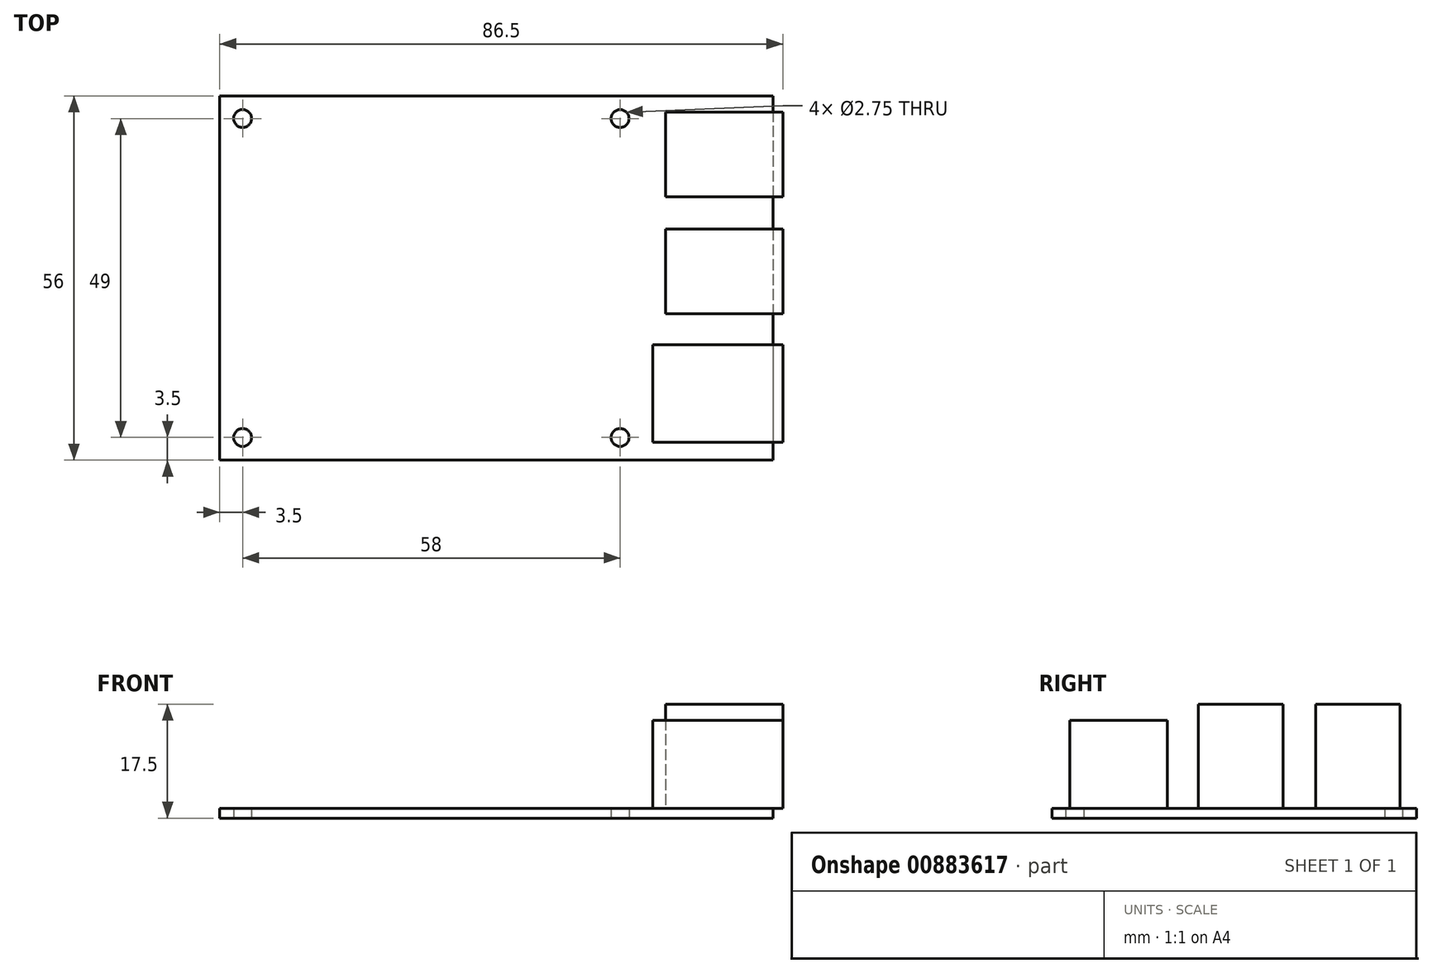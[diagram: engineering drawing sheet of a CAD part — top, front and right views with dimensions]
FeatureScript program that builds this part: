
annotation { "Feature Type Name" : "Feature", "Feature Type Description" : "" }
export const myFeature = defineFeature(function(context is Context, id is Id, definition is map)
    precondition{}
    {
        {
            var Q0;
            Q0=qCreatedBy(makeId("Top.planeOp"),FACE);
            var sketch = newSketch(context, id + "F0", { "sketchPlane" : qUnion([Q0])});
            skLineSegment(sketch, "E0.bottom", {"start": v(0, 56) * mm, "end": v(85, 56) * mm});
            skLineSegment(sketch, "E0.top", {"start": v(0, 0) * mm, "end": v(85, 0) * mm});
            skLineSegment(sketch, "E0.left", {"start": v(0, 56) * mm, "end": v(0, 0) * mm});
            skLineSegment(sketch, "E0.right", {"start": v(85, 56) * mm, "end": v(85, 0) * mm});
            skCircle(sketch, "E1", {"center": v(3.5, 52.5) * mm, "radius": 1.38 * mm});
            skCircle(sketch, "E2", {"center": v(3.5, 3.5) * mm, "radius": 1.38 * mm});
            skCircle(sketch, "E3", {"center": v(61.5, 3.5) * mm, "radius": 1.37 * mm});
            skCircle(sketch, "E4", {"center": v(61.5, 52.5) * mm, "radius": 1.37 * mm});
            skLineSegment(sketch, "E5", {"start": v(3.5, 52.5) * mm, "end": v(61.5, 52.5) * mm, "construction": true});
            skLineSegment(sketch, "E6", {"start": v(61.5, 52.5) * mm, "end": v(61.5, 3.5) * mm, "construction": true});
            skSolve(sketch);
        }
        {
            var Q0;
            {var subQ15=sQuery(id+"F0.wireOp",EDGE,"E0.bottom");Q0=makeQuery(id+"F0.imprint","IMPRINT",FACE,{"disambiguationData":[TD([[makeQuery(id+"F0.imprint","IMPRINT",EDGE,{"derivedFrom":subQ15}),-1.0]])]});}
            var Q1;
            {var subQ5=sQuery(id+"F0.wireOp",EDGE,"uZb7aYxC-zsMW-nidB-drXf-hPC2NGSKKxi8.left");Q1=makeQuery(id+"F0.imprint","IMPRINT",FACE,{"disambiguationData":[TD([[makeQuery(id+"F0.imprint","IMPRINT",EDGE,{"derivedFrom":subQ5}),-1.0]])]});}
            var Q2;
            {var subQ5=sQuery(id+"F0.wireOp",EDGE,"CbbDYCzH-yuqy-8fo1-o1oq-vRqS8r6QZwP0.left");Q2=makeQuery(id+"F0.imprint","IMPRINT",FACE,{"disambiguationData":[TD([[makeQuery(id+"F0.imprint","IMPRINT",EDGE,{"derivedFrom":subQ5}),-1.0]])]});}
            var Q3;
            {var subQ5=sQuery(id+"F0.wireOp",EDGE,"Eq4EePK6-Jx8p-WvZy-9MCs-DtvyUnJVBhWV.left");Q3=makeQuery(id+"F0.imprint","IMPRINT",FACE,{"disambiguationData":[TD([[makeQuery(id+"F0.imprint","IMPRINT",EDGE,{"derivedFrom":subQ5}),-1.0]])]});}
            extrude(context, id + "F1", {"entities" : qUnion([Q0, Q1, Q2, Q3]), "depth" : 1.5 * mm, "offsetDistance" : 25 * mm});
        }
        {
            var Q0;
            Q0=makeQuery(id+"F1.opExtrude","CAP_FACE",FACE,{"disambiguationData":[OSD([sQuery(id+"F0.wireOp",EDGE,"E0.bottom"),sQuery(id+"F0.wireOp",EDGE,"E0.top"),sQuery(id+"F0.wireOp",EDGE,"E0.left"),sQuery(id+"F0.wireOp",EDGE,"E0.right"),sQuery(id+"F0.wireOp",EDGE,"E1"),sQuery(id+"F0.wireOp",EDGE,"E2"),sQuery(id+"F0.wireOp",EDGE,"E3"),sQuery(id+"F0.wireOp",EDGE,"E4")])],"isStart":false});
            cPlane(context, id + "F2", {"entities" : qUnion([Q0]), "cplaneType" : CPlaneType.OFFSET, "offset" : 0 * mm, "width" : 150 * mm, "height" : 150 * mm});
        }
        {
            var Q0;
            Q0=qCreatedBy(id+"F2.planeOp",FACE);
            var sketch = newSketch(context, id + "F3", { "sketchPlane" : qUnion([Q0])});
            skLineSegment(sketch, "E7.bottom", {"start": v(68.5, 53.5) * mm, "end": v(86.5, 53.5) * mm});
            skLineSegment(sketch, "E7.top", {"start": v(68.5, 40.5) * mm, "end": v(86.5, 40.5) * mm});
            skLineSegment(sketch, "E7.left", {"start": v(68.5, 53.5) * mm, "end": v(68.5, 40.5) * mm});
            skLineSegment(sketch, "E7.right", {"start": v(86.5, 53.5) * mm, "end": v(86.5, 40.5) * mm});
            skLineSegment(sketch, "E8.bottom", {"start": v(68.5, 35.5) * mm, "end": v(86.5, 35.5) * mm});
            skLineSegment(sketch, "E8.top", {"start": v(68.5, 22.5) * mm, "end": v(86.5, 22.5) * mm});
            skLineSegment(sketch, "E8.left", {"start": v(68.5, 35.5) * mm, "end": v(68.5, 22.5) * mm});
            skLineSegment(sketch, "E8.right", {"start": v(86.5, 35.5) * mm, "end": v(86.5, 22.5) * mm});
            skLineSegment(sketch, "E9.bottom", {"start": v(66.5, 17.75) * mm, "end": v(86.5, 17.75) * mm});
            skLineSegment(sketch, "E9.top", {"start": v(66.5, 2.75) * mm, "end": v(86.5, 2.75) * mm});
            skLineSegment(sketch, "E9.left", {"start": v(66.5, 17.75) * mm, "end": v(66.5, 2.75) * mm});
            skLineSegment(sketch, "E9.right", {"start": v(86.5, 17.75) * mm, "end": v(86.5, 2.75) * mm});
            skPoint(sketch, "E10", {"position": v(68.5, 47) * mm});
            skPoint(sketch, "E11", {"position": v(68.5, 29) * mm});
            skPoint(sketch, "E12", {"position": v(66.5, 10.25) * mm});
            skSolve(sketch);
        }
        {
            var Q0;
            Q0=makeQuery(id+"F3.imprint","IMPRINT",FACE,{"disambiguationData":[TD([[makeQuery(id+"F3.imprint","IMPRINT",EDGE,{"derivedFrom":sQuery(id+"F3.wireOp",EDGE,"E7.bottom")}),-1.0]])]});
            var Q1;
            Q1=makeQuery(id+"F3.imprint","IMPRINT",FACE,{"disambiguationData":[TD([[makeQuery(id+"F3.imprint","IMPRINT",EDGE,{"derivedFrom":sQuery(id+"F3.wireOp",EDGE,"E8.bottom")}),-1.0]])]});
            extrude(context, id + "F4", {"entities" : qUnion([Q0, Q1]), "operationType" : NewBodyOperationType.ADD, "depth" : 16 * mm, "offsetDistance" : 25 * mm});
        }
        {
            var Q0;
            Q0=makeQuery(id+"F3.imprint","IMPRINT",FACE,{"disambiguationData":[TD([[makeQuery(id+"F3.imprint","IMPRINT",EDGE,{"derivedFrom":sQuery(id+"F3.wireOp",EDGE,"E9.bottom")}),-1.0]])]});
            extrude(context, id + "F5", {"entities" : qUnion([Q0]), "operationType" : NewBodyOperationType.ADD, "depth" : 13.5 * mm, "offsetDistance" : 25 * mm});
        }
    });
